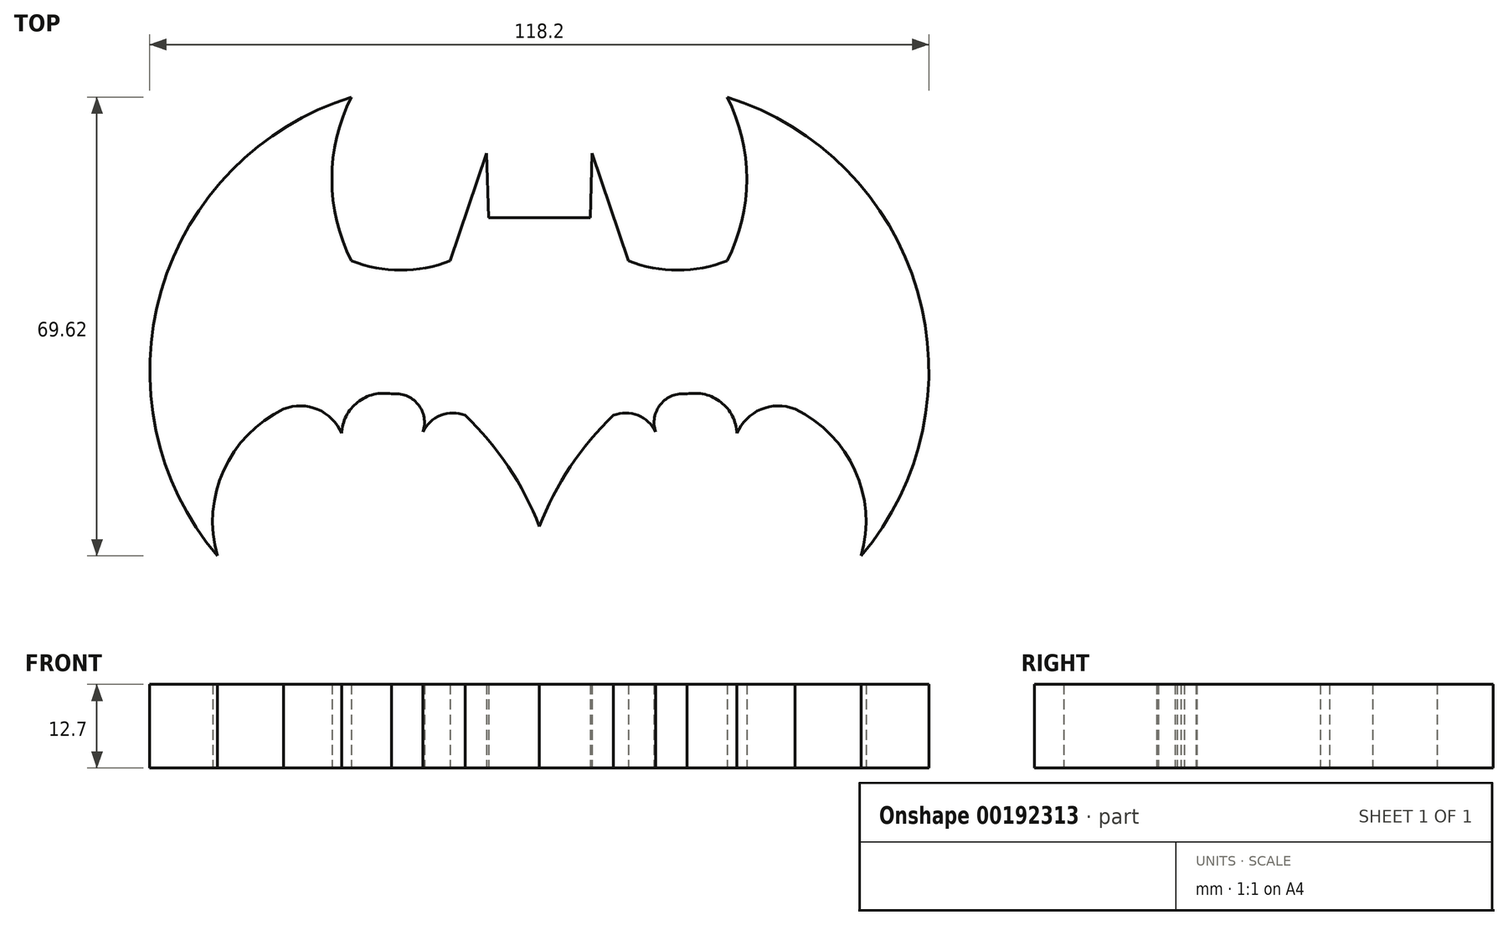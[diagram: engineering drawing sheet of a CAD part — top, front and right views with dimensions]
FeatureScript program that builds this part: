
annotation { "Feature Type Name" : "Feature", "Feature Type Description" : "" }
export const myFeature = defineFeature(function(context is Context, id is Id, definition is map)
    precondition{}
    {
        {
            var Q0;
            Q0=qCreatedBy(makeId("Top.planeOp"),FACE);
            var sketch = newSketch(context, id + "F0", { "sketchPlane" : qUnion([Q0])});
            skLineSegment(sketch, "E0", {"start": v(0, 0) * mm, "end": v(-7.71, 0) * mm});
            skLineSegment(sketch, "E1", {"start": v(-7.71, 0) * mm, "end": v(-8.02, 9.8) * mm});
            skLineSegment(sketch, "E2", {"start": v(-8.02, 9.8) * mm, "end": v(-13.5, -6.53) * mm});
            skArc(sketch, "E3", {"start": v(-28.5, -6.53) * mm, "mid": v(-21, -7.94) * mm, "end": v(-13.5, -6.53) * mm});
            skArc(sketch, "E4", {"start": v(-28.5, 18.32) * mm, "mid": v(-31.47, 5.9) * mm, "end": v(-28.5, -6.53) * mm});
            skArc(sketch, "E5", {"start": v(-28.5, 18.32) * mm, "mid": v(-57.35, -11.03) * mm, "end": v(-48.84, -51.3) * mm});
            skArc(sketch, "E6", {"start": v(-38.78, -29.03) * mm, "mid": v(-47.89, -38.32) * mm, "end": v(-48.84, -51.3) * mm});
            skArc(sketch, "E7", {"start": v(-29.99, -32.71) * mm, "mid": v(-33.63, -29.07) * mm, "end": v(-38.78, -29.03) * mm});
            skArc(sketch, "E8", {"start": v(-22.4, -26.74) * mm, "mid": v(-27.56, -27.99) * mm, "end": v(-29.99, -32.71) * mm});
            skArc(sketch, "E9", {"start": v(-17.84, -32.96) * mm, "mid": v(-18.26, -28.49) * mm, "end": v(-22.4, -26.74) * mm});
            skArc(sketch, "E10", {"start": v(-11.25, -29.97) * mm, "mid": v(-15.18, -30.07) * mm, "end": v(-17.84, -32.96) * mm});
            skArc(sketch, "E11", {"start": v(0, -46.86) * mm, "mid": v(-4.7, -37.8) * mm, "end": v(-11.25, -29.97) * mm});
            skArc(sketch, "E12.0.MirrorCS", {"start": v(11.25, -29.97) * mm, "mid": v(15.18, -30.07) * mm, "end": v(17.84, -32.96) * mm});
            skLineSegment(sketch, "E12.1.MirrorCS", {"start": v(7.71, 0) * mm, "end": v(8.02, 9.8) * mm});
            skArc(sketch, "E12.2.MirrorCS", {"start": v(17.84, -32.96) * mm, "mid": v(18.26, -28.49) * mm, "end": v(22.4, -26.74) * mm});
            skArc(sketch, "E12.3.MirrorCS", {"start": v(38.78, -29.03) * mm, "mid": v(47.89, -38.32) * mm, "end": v(48.84, -51.3) * mm});
            skLineSegment(sketch, "E12.4.MirrorCS", {"start": v(8.02, 9.8) * mm, "end": v(13.5, -6.53) * mm});
            skArc(sketch, "E12.5.MirrorCS", {"start": v(28.5, -6.53) * mm, "mid": v(21, -7.94) * mm, "end": v(13.5, -6.53) * mm});
            skArc(sketch, "E12.6.MirrorCS", {"start": v(29.99, -32.71) * mm, "mid": v(33.63, -29.07) * mm, "end": v(38.78, -29.03) * mm});
            skArc(sketch, "E12.7.MirrorCS", {"start": v(22.4, -26.74) * mm, "mid": v(27.56, -27.99) * mm, "end": v(29.99, -32.71) * mm});
            skArc(sketch, "E13.0.MirrorCS", {"start": v(0, -46.86) * mm, "mid": v(4.7, -37.8) * mm, "end": v(11.25, -29.97) * mm});
            skArc(sketch, "E14.0.MirrorCS", {"start": v(28.5, 18.32) * mm, "mid": v(57.35, -11.03) * mm, "end": v(48.84, -51.3) * mm});
            skArc(sketch, "E15.0.MirrorCS", {"start": v(28.5, 18.32) * mm, "mid": v(31.47, 5.9) * mm, "end": v(28.5, -6.53) * mm});
            skLineSegment(sketch, "E16.0.MirrorCS", {"start": v(0, 0) * mm, "end": v(7.71, 0) * mm});
            skSolve(sketch);
        }
        {
            var Q0;
            Q0=makeQuery(id+"F0.imprint","IMPRINT",FACE,{"disambiguationData":[TD([[makeQuery(id+"F0.imprint","IMPRINT",EDGE,{"derivedFrom":sQuery(id+"F0.wireOp",EDGE,"E0")}),1.0]])]});
            extrude(context, id + "F1", {"entities" : qUnion([Q0]), "depth" : 12.7 * mm});
        }
    });
